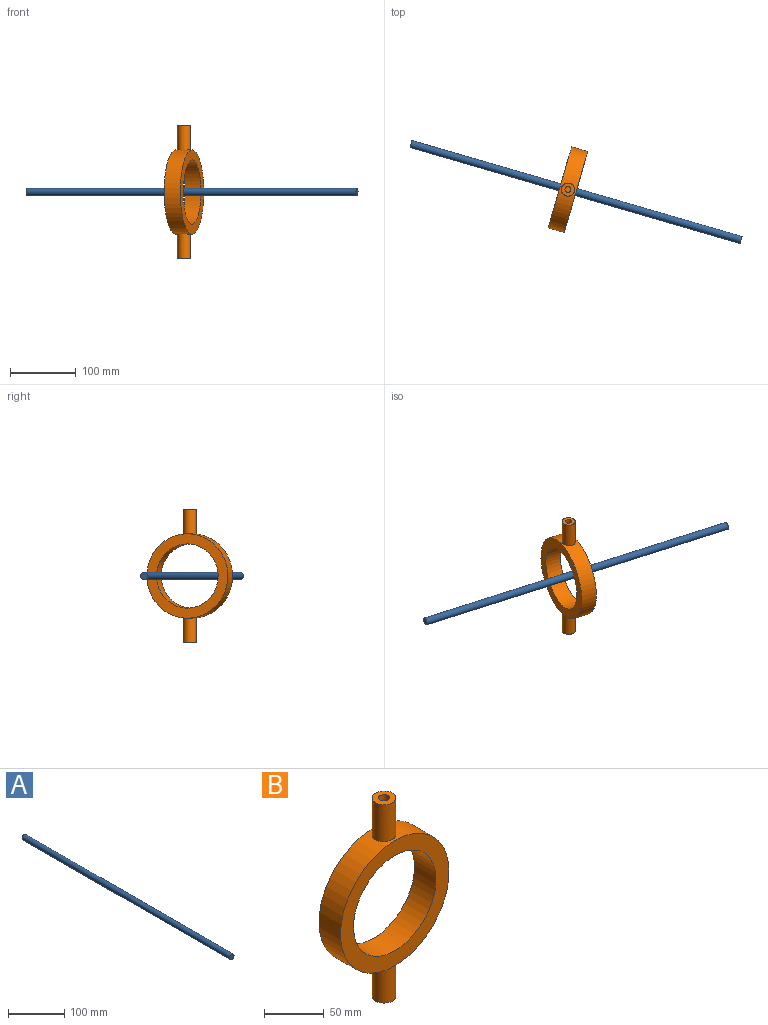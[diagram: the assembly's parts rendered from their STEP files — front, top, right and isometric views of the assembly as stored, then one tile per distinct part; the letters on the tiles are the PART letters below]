
ASSEMBLY  parts=2 mates=1
PART A: 3 faces, bbox 11.1x521x11.1 mm
  f0: cylinder r=5.54mm len=521.01mm, axis (0,1,0), area 18134.7mm2, adj f1,f2
  f1: plane 11.08x11.08mm, normal (0,-1,0), area 96.4mm2, adj f0
  f2: plane 11.08x11.08mm, normal (0,1,0), area 96.4mm2, adj f0
PART B: 12 faces, bbox 128x25.4x202.7 mm
  f0: cylinder r=63.99mm len=127.99mm, axis (0,1,0), area 9590.4mm2, adj f1,f2,f5,f7
  f1: plane 127.99x127.99mm, normal (0,-1,0), area 5423.2mm2, adj f0,f11
  f2: plane 127.99x127.99mm, normal (0,1,0), area 5423.2mm2, adj f0,f11
  f3: cylinder r=4.56mm len=37.52mm, axis (0,0,-1), area 1072.7mm2, adj f4,f9
  f4: plane 19.85x19.85mm, normal (0,0,-1), area 244mm2, adj f3,f5
  f5: cylinder r=9.92mm len=38.13mm, axis (0,0,-1), area 2353mm2, adj f0,f4
  f6: plane 19.85x19.85mm, normal (0,0,1), area 244mm2, adj f7,f8
  f7: cylinder r=9.92mm len=38.13mm, axis (0,0,-1), area 2352.9mm2, adj f0,f6
  f8: cylinder r=4.56mm len=37.52mm, axis (0,0,-1), area 1072.7mm2, adj f6,f10
  f9: cylinder r=63.99mm len=9.12mm, axis (0,1,0), area 65.4mm2, adj f3
  f10: cylinder r=63.99mm len=9.12mm, axis (0,1,0), area 65.4mm2, adj f8
  f11: cylinder r=48.67mm len=97.35mm, axis (0,-1,0), area 7767.8mm2, adj f1,f2
PLACE A rot(axis=(0,0,1),73.8deg) t=(151.78,-66.45,-23.07)mm
PLACE B rot(axis=(0.6,-0.8,0),180deg) t=(139.59,-62.91,-23.07)mm
MATE revolute B.f11 <-> A.f0  axis (0.96,-0.28,0) through (151.78,-66.45,-23.07)mm
